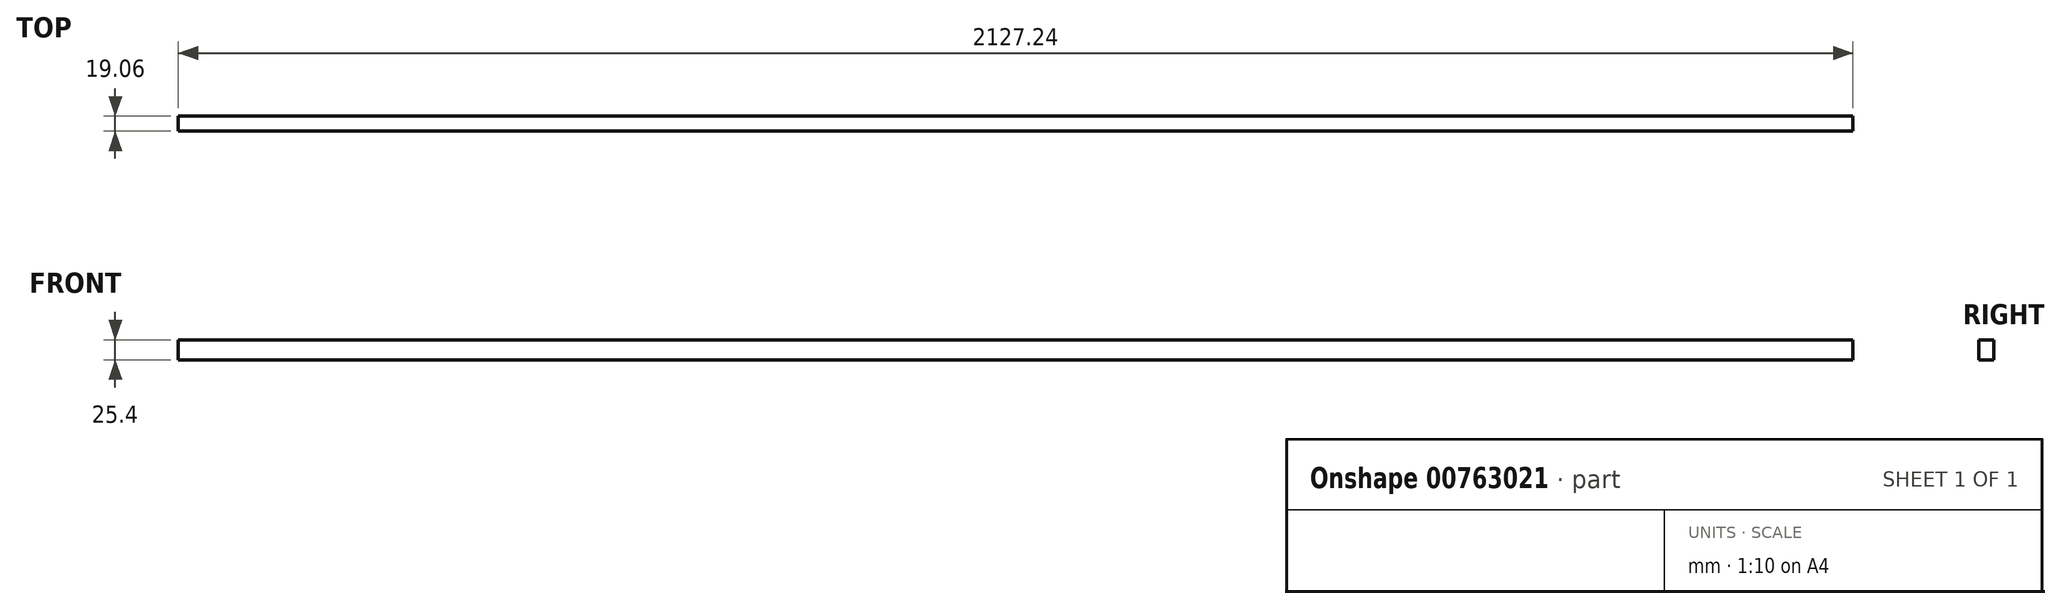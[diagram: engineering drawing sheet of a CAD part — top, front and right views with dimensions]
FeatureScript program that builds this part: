
annotation { "Feature Type Name" : "Feature", "Feature Type Description" : "" }
export const myFeature = defineFeature(function(context is Context, id is Id, definition is map)
    precondition{}
    {
        {
            var Q0;
            Q0=qCreatedBy(makeId("Top.planeOp"),FACE);
            var sketch = newSketch(context, id + "F0", { "sketchPlane" : qUnion([Q0])});
            skLineSegment(sketch, "E0.bottom", {"start": v(-1063.62, 9.53) * mm, "end": v(1063.63, 9.53) * mm});
            skLineSegment(sketch, "E0.top", {"start": v(-1063.62, -9.53) * mm, "end": v(1063.63, -9.53) * mm});
            skLineSegment(sketch, "E0.left", {"start": v(-1063.62, 9.52) * mm, "end": v(-1063.62, -9.53) * mm});
            skLineSegment(sketch, "E0.right", {"start": v(1063.63, 9.53) * mm, "end": v(1063.63, -9.53) * mm});
            skPoint(sketch, "E0.middle", {"position": v(0, 0) * mm});
            skSolve(sketch);
        }
        {
            var Q0;
            Q0=makeQuery(id+"F0.imprint","IMPRINT",FACE,{"disambiguationData":[TD([[makeQuery(id+"F0.imprint","IMPRINT",EDGE,{"derivedFrom":sQuery(id+"F0.wireOp",EDGE,"E0.bottom")}),-1.0]])]});
            extrude(context, id + "F1", {"entities" : qUnion([Q0]), "depth" : 25.4 * mm, "offsetDistance" : 25.4 * mm});
        }
    });
